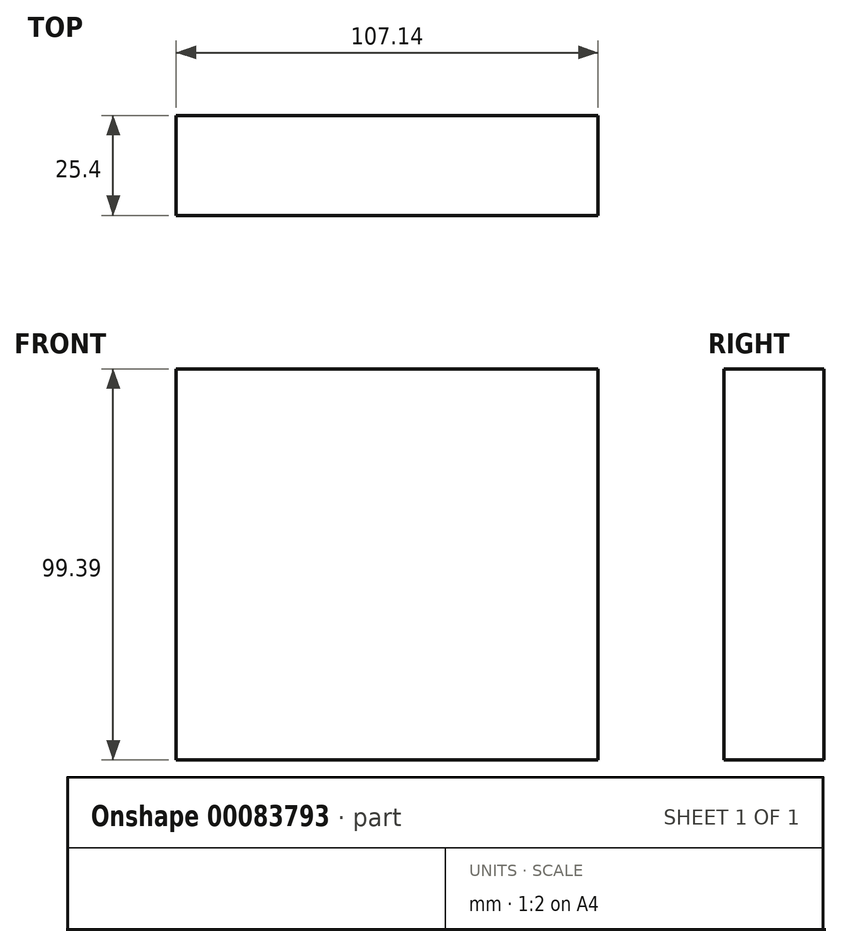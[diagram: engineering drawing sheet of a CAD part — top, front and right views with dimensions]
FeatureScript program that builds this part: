
annotation { "Feature Type Name" : "Feature", "Feature Type Description" : "" }
export const myFeature = defineFeature(function(context is Context, id is Id, definition is map)
    precondition{}
    {
        {
            var Q0;
            Q0=qCreatedBy(makeId("Front.planeOp"),FACE);
            var sketch = newSketch(context, id + "F0", { "sketchPlane" : qUnion([Q0])});
            skLineSegment(sketch, "E0.bottom", {"start": v(-41.68, 45.45) * mm, "end": v(65.46, 45.45) * mm});
            skLineSegment(sketch, "E0.top", {"start": v(-41.68, -53.94) * mm, "end": v(65.46, -53.94) * mm});
            skLineSegment(sketch, "E0.left", {"start": v(-41.68, 45.45) * mm, "end": v(-41.68, -53.94) * mm});
            skLineSegment(sketch, "E0.right", {"start": v(65.46, 45.45) * mm, "end": v(65.46, -53.94) * mm});
            skSolve(sketch);
        }
        {
            var Q0;
            Q0=makeQuery(id+"F0.imprint","IMPRINT",FACE,{"disambiguationData":[TD([[makeQuery(id+"F0.imprint","IMPRINT",EDGE,{"derivedFrom":sQuery(id+"F0.wireOp",EDGE,"E0.bottom")}),-1.0]])]});
            extrude(context, id + "F1", {"entities" : qUnion([Q0]), "depth" : 25.4 * mm, "offsetDistance" : 25.4 * mm});
        }
    });
